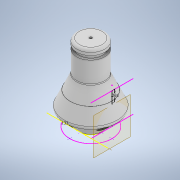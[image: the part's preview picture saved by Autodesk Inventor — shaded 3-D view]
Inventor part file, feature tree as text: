
AUTODESK INVENTOR PART (.ipt)
format: ipt  version: 2020 (Build 240168000, 168)  size: 295,424 bytes
history: native  units: in
note: dims shown in document units (in); Inventor stores cm internally (conversion verified against a paired STEP export)
features: sketch x6, hole x4, plane x2, fillet x2, revolve x1, pattern_circular x1
ambient origin geometry x8: Origin, YZ Plane, XZ Plane, XY Plane, X Axis, Y Axis, Z Axis, Center Point
bodies: Solid1 (feature_tree)
feature tree (16):
  revolve  "Revolution1"  [1 undecoded]
  hole  "Hole4"  [1 undecoded]
  hole  "Hole8"  [1 undecoded]
  sketch  "Sketch13"  dims[d2=90.0deg d3=0.057in]
  plane  "Work Plane6"
  sketch  "Sketch14"  dims[d4=0.095in d5=0.125in]
  sketch  "Sketch29"  dims[d24=0.4466in d25=0.125in]
  plane  "Work Plane5"
  sketch  "Sketch30"  dims[d54=0.3779in d72=0.3779in d83=0.75in d84=0.75in d85=0.0625in d86=0.75in d87=0.375in d88=0.25in d89=0.5635in d90=0.95in d91=0.8108in d92=0.2645in d121=0.196in d122=0.25in d123=0.375in d124=0.25in d125=0.5635in d126=0.25in d127=0.0in d137=0.3779in d155=0.3779in d173=0.3779in d191=0.3779in d221=0.3779in d239=0.3779in d253=45.0deg d254=0.1325in d255=0.0625in d256=0.25in d257=0.375in d258=0.25in d259=0.5635in d260=0.775in d261=0.0in d262=0.211in d263=0.25in d264=0.375in d265=0.25in d266=0.5635in d267=0.25in d268=0.0in d269=1.5748in d270=1.3743in d272=0.0625in d273=0.0625in]
  hole  "Hole9"  [1 undecoded]
  hole  "Hole10"  [1 undecoded]
  pattern_circular  "Circular Pattern7"  [2 undecoded]
  fillet  "Fillet1"  Radius=0.75in
  fillet  "Fillet2"  Radius=0.75in
  sketch  "Sketch12"  dims[d0=0.3328in d1=0.5in]
  sketch  "Sketch16"  dims[d6=90.0deg d23=0.65in]
note: 7 required parameter values undecoded (feature->parameter linkage not recoverable at this tier; creation-order binding heuristic only, values carry confidence <= 0.55)